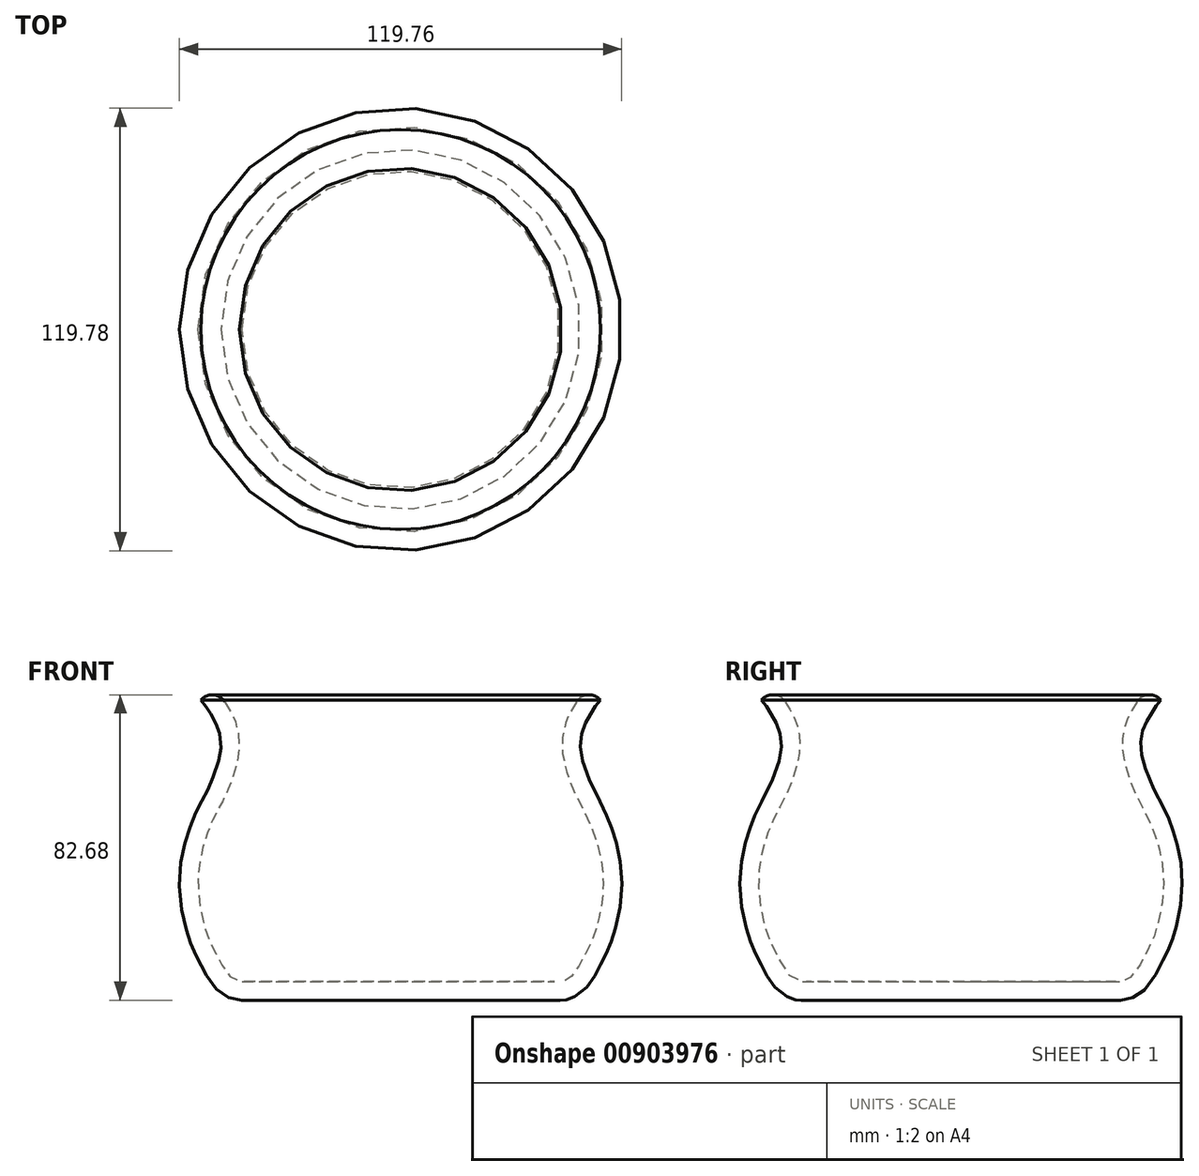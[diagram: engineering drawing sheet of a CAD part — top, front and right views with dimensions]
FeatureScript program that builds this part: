
annotation { "Feature Type Name" : "Feature", "Feature Type Description" : "" }
export const myFeature = defineFeature(function(context is Context, id is Id, definition is map)
    precondition{}
    {
        {
            var Q0;
            Q0=qCreatedBy(makeId("Front.planeOp"),FACE);
            var sketch = newSketch(context, id + "F0", { "sketchPlane" : qUnion([Q0])});
            skFitSpline(sketch, "E0", {"points": [v(-43.61, 32.65) * mm, v(-40.47, 28.61) * mm, v(-37.33, 22.55) * mm, v(-36.66, 13.58) * mm, v(-40.24, 2.8) * mm, v(-43.26, -2.99) * mm, v(-46.78, -13.31) * mm, v(-47.29, -25.15) * mm, v(-44.93, -35.14) * mm, v(-42.13, -41) * mm, v(-35.63, -47.45) * mm], "startDerivative": vector(55.55, -45.55) * mm, "endDerivative": vector(99.5, 0) * mm});
            skFitSpline(sketch, "E1.1", {"points": [v(-46.78, 28.79) * mm, v(-46.65, 28.67) * mm, v(-46.4, 28.45) * mm, v(-46.07, 28.07) * mm, v(-45.76, 27.64) * mm, v(-45.48, 27.2) * mm, v(-45.24, 26.83) * mm, v(-45.03, 26.49) * mm, v(-44.85, 26.19) * mm, v(-44.65, 25.87) * mm, v(-44.41, 25.47) * mm, v(-44.13, 25) * mm, v(-43.85, 24.55) * mm, v(-43.5, 23.94) * mm, v(-43.07, 23.2) * mm, v(-42.62, 22.31) * mm, v(-42.3, 21.6) * mm, v(-42.1, 21.03) * mm, v(-41.9, 20.48) * mm, v(-41.7, 19.75) * mm, v(-41.53, 18.83) * mm, v(-41.39, 17.53) * mm, v(-41.38, 16.12) * mm, v(-41.53, 14.78) * mm, v(-41.66, 13.98) * mm, v(-41.82, 13.14) * mm, v(-42.08, 12.05) * mm, v(-42.6, 10.24) * mm, v(-43.24, 8.42) * mm, v(-43.94, 6.72) * mm, v(-44.38, 5.74) * mm, v(-44.72, 5.02) * mm, v(-45.05, 4.34) * mm, v(-45.46, 3.54) * mm, v(-45.97, 2.6) * mm, v(-46.51, 1.62) * mm, v(-47.09, 0.55) * mm, v(-47.59, -0.45) * mm, v(-48, -1.32) * mm, v(-48.41, -2.22) * mm, v(-48.92, -3.41) * mm, v(-49.52, -4.93) * mm, v(-50.1, -6.54) * mm, v(-50.64, -8.2) * mm, v(-51.13, -9.93) * mm, v(-51.56, -11.7) * mm, v(-52.04, -14.1) * mm, v(-52.44, -17.09) * mm, v(-52.6, -20.67) * mm, v(-52.45, -24.23) * mm, v(-52.02, -27.77) * mm, v(-51.46, -30.6) * mm, v(-50.93, -32.76) * mm, v(-50.5, -34.31) * mm, v(-50.1, -35.53) * mm, v(-49.77, -36.47) * mm, v(-49.43, -37.37) * mm, v(-49, -38.43) * mm, v(-48.46, -39.59) * mm, v(-47.92, -40.67) * mm, v(-47.47, -41.54) * mm, v(-47.1, -42.25) * mm, v(-46.87, -42.7) * mm, v(-46.68, -43.08) * mm, v(-46.49, -43.46) * mm, v(-46.22, -44) * mm, v(-45.86, -44.7) * mm, v(-45.31, -45.74) * mm, v(-44.5, -47.13) * mm, v(-43.4, -48.6) * mm, v(-42.29, -49.76) * mm, v(-41.3, -50.6) * mm, v(-40.12, -51.35) * mm, v(-38.76, -51.96) * mm, v(-37.24, -52.36) * mm, v(-36.17, -52.45) * mm, v(-35.63, -52.45) * mm]});
            skLineSegment(sketch, "E2", {"start": v(-46.78, 28.79) * mm, "end": v(-43.61, 32.65) * mm});
            skLineSegment(sketch, "E3", {"start": v(-35.63, -47.45) * mm, "end": v(7.3, -47.45) * mm});
            skLineSegment(sketch, "E4", {"start": v(-35.63, -52.45) * mm, "end": v(7.3, -52.45) * mm});
            skLineSegment(sketch, "E5", {"start": v(7.3, -52.45) * mm, "end": v(7.3, -47.45) * mm});
            skSolve(sketch);
        }
        {
            var Q0;
            Q0=makeQuery(id+"F0.imprint","IMPRINT",FACE,{"disambiguationData":[TD([[makeQuery(id+"F0.imprint","IMPRINT",EDGE,{"derivedFrom":sQuery(id+"F0.wireOp",EDGE,"E0")}),-1.0]])]});
            var Q1;
            Q1=sQuery(id+"F0.wireOp",EDGE,"E5");
            revolve(context, id + "F1", {"surfaceOperationType" : NewSurfaceOperationType.NEW, "entities" : qUnion([Q0]), "axis" : qUnion([Q1]), "revolveType" : RevolveType.FULL});
        }
        {
            var Q0;
            Q0=makeQuery(id+"F1.opRevolve","SWEPT_EDGE",EDGE,{"disambiguationData":[OSD([sQuery(id+"F0.wireOp",EDGE,"E0"),sQuery(id+"F0.wireOp",EDGE,"E2")])]});
            fillet(context, id + "F2", {"entities" : qUnion([Q0]), "radius" : 4 * mm, "tangentPropagation" : true, "allowEdgeOverflow" : false});
        }
    });
